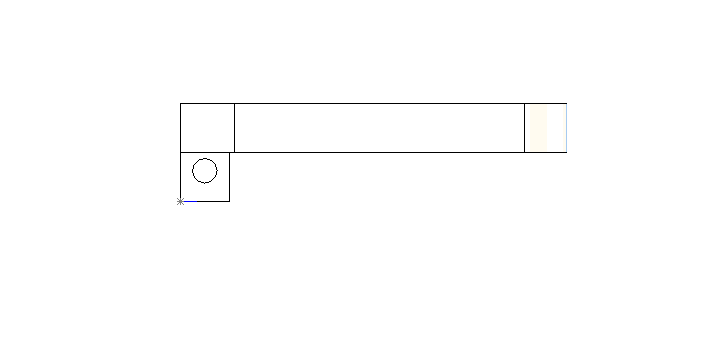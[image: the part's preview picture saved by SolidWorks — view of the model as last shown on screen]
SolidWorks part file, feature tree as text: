
SOLIDWORKS PART (.sldprt)
format: sldprt  version: not decoded by parser v0  size: 250,880 bytes
history: native  units: mm
features: sketch x3, extrude x2, cut_extrude x1 (+11 scaffold rows collapsed)
feature tree (17):
  scaffold x11  (default folders/planes/origin — collapsed)
  sketch  "Sketch1"  dims[D7=2.54mm D1=3.175mm D2=3.175mm D3=3.175mm D4=25.4mm D5=25.4mm D6=50.8mm]
  extrude  "Extrude1"  Depth=50.8mm
  sketch  "Sketch2"  dims[c1.D5=~18.874628mm c1.D6=~21.862086mm c1.D7=~18.840673mm c2.D6=~18.840673mm c2.D1=177.8mm c2.D2=3.175mm c2.D3=27.94mm c2.D4=3.175mm c2.D5=~150.427197mm c3.D5=~179.857705deg c3.D7=~150.427197mm c4.D7=~179.857705deg c5.D7=~150.427197mm c6.D7=~179.857705deg c6.D5=3.175mm c6.D6=~3.432149mm]
  extrude  "Extrude2"  Depth=25.4mm
  sketch  "Sketch3"  dims[c1.D1=12.7mm c1.D3=12.7mm c1.D2=15.875mm c2.D3=12.7mm]
  cut_extrude  "Cut-Extrude1"  [1 undecoded]
decode coverage: 5 of 6 modeling features carry decoded parameters
note: ~ marks probable driven/reference dimensions
note: 1 parameter value undecoded
note: suppression state not decoded; provenance and decode notes live in map.json
